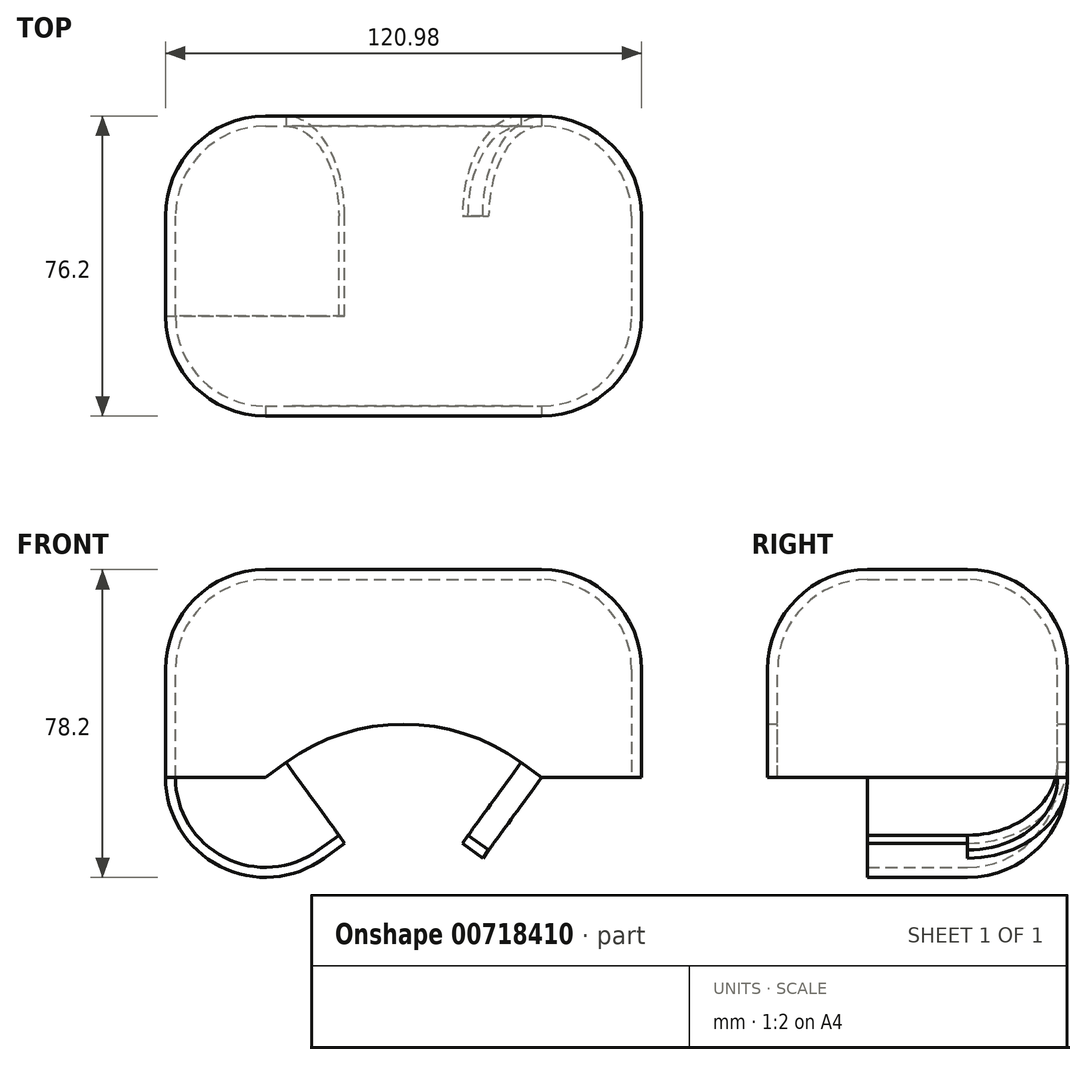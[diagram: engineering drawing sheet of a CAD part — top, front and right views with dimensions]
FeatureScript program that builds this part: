
annotation { "Feature Type Name" : "Feature", "Feature Type Description" : "" }
export const myFeature = defineFeature(function(context is Context, id is Id, definition is map)
    precondition{}
    {
        {
            var Q0;
            Q0=qCreatedBy(makeId("Front.planeOp"),FACE);
            var sketch = newSketch(context, id + "F0", { "sketchPlane" : qUnion([Q0])});
            skLineSegment(sketch, "E0", {"start": v(-60.49, 58.68) * mm, "end": v(60.49, 58.68) * mm});
            skLineSegment(sketch, "E1", {"start": v(60.49, 58.68) * mm, "end": v(60.49, -44) * mm});
            skLineSegment(sketch, "E2", {"start": v(60.49, -44) * mm, "end": v(0, 0) * mm});
            skLineSegment(sketch, "E3", {"start": v(0, 0) * mm, "end": v(-60.49, -44) * mm});
            skLineSegment(sketch, "E4", {"start": v(-60.49, -44) * mm, "end": v(-60.49, 58.68) * mm});
            skSolve(sketch);
        }
        {
            var Q0;
            Q0=makeQuery(id+"F0.imprint","IMPRINT",FACE,{"disambiguationData":[TD([[makeQuery(id+"F0.imprint","IMPRINT",EDGE,{"derivedFrom":sQuery(id+"F0.wireOp",EDGE,"E0")}),-1.0]])]});
            extrude(context, id + "F1", {"entities" : qUnion([Q0]), "depth" : 76.2 * mm, "offsetDistance" : 25.4 * mm});
        }
        {
            var Q0;
            Q0=makeQuery(id+"F1.opExtrude","SWEPT_FACE",FACE,{"disambiguationData":[OSD([sQuery(id+"F0.wireOp",EDGE,"E3")])]});
            var Q1;
            Q1=makeQuery(id+"F1.opExtrude","SWEPT_FACE",FACE,{"disambiguationData":[OSD([sQuery(id+"F0.wireOp",EDGE,"E1")])]});
            var Q2;
            Q2=makeQuery(id+"F1.opExtrude","SWEPT_FACE",FACE,{"disambiguationData":[OSD([sQuery(id+"F0.wireOp",EDGE,"E4")])]});
            var Q3;
            Q3=makeQuery(id+"F1.opExtrude","CAP_FACE",FACE,{"disambiguationData":[OSD([sQuery(id+"F0.wireOp",EDGE,"E0"),sQuery(id+"F0.wireOp",EDGE,"E1"),sQuery(id+"F0.wireOp",EDGE,"E2"),sQuery(id+"F0.wireOp",EDGE,"E3"),sQuery(id+"F0.wireOp",EDGE,"E4")])],"isStart":false});
            var Q4;
            Q4=makeQuery(id+"F1.opExtrude","CAP_FACE",FACE,{"disambiguationData":[OSD([sQuery(id+"F0.wireOp",EDGE,"E0"),sQuery(id+"F0.wireOp",EDGE,"E1"),sQuery(id+"F0.wireOp",EDGE,"E2"),sQuery(id+"F0.wireOp",EDGE,"E3"),sQuery(id+"F0.wireOp",EDGE,"E4")])],"isStart":true});
            var Q5;
            Q5=makeQuery(id+"F1.opExtrude","CAP_EDGE",EDGE,{"disambiguationData":[OSD([sQuery(id+"F0.wireOp",EDGE,"E1")])],"isStart":true});
            var Q6;
            Q6=makeQuery(id+"F1.opExtrude","CAP_EDGE",EDGE,{"disambiguationData":[OSD([sQuery(id+"F0.wireOp",EDGE,"E4")])],"isStart":true});
            var Q7;
            Q7=makeQuery(id+"F1.opExtrude","CAP_EDGE",EDGE,{"disambiguationData":[OSD([sQuery(id+"F0.wireOp",EDGE,"E4")])],"isStart":false});
            var Q8;
            Q8=makeQuery(id+"F1.opExtrude","CAP_EDGE",EDGE,{"disambiguationData":[OSD([sQuery(id+"F0.wireOp",EDGE,"E2")])],"isStart":true});
            var Q9;
            Q9=makeQuery(id+"F1.opExtrude","CAP_EDGE",EDGE,{"disambiguationData":[OSD([sQuery(id+"F0.wireOp",EDGE,"E3")])],"isStart":true});
            var Q10;
            Q10=makeQuery(id+"F1.opExtrude","SWEPT_EDGE",EDGE,{"disambiguationData":[OSD([sQuery(id+"F0.wireOp",EDGE,"E2"),sQuery(id+"F0.wireOp",EDGE,"E3")])]});
            fillet(context, id + "F2", {"entities" : qUnion([Q0, Q1, Q2, Q3, Q4, Q5, Q6, Q7, Q8, Q9, Q10]), "radius" : 25.4 * mm, "tangentPropagation" : true, "allowEdgeOverflow" : false});
        }
        {
            var Q0;
            {var subQ0=sQuery(id+"F0.wireOp",EDGE,"E3");var subQ1=sQuery(id+"F0.wireOp",EDGE,"E2");Q0=makeQuery(id+"F2.opFillet","BLEND_FACE",FACE,{"disambiguationData":[OSD([subQ1,subQ0]),TDD([makeQuery(id+"F1.opExtrude","SWEPT_EDGE",EDGE,{"disambiguationData":[OSD([subQ1,subQ0])]})])]});}
            var Q1;
            {var subQ0=sQuery(id+"F0.wireOp",EDGE,"E3");var subQ1=sQuery(id+"F0.wireOp",EDGE,"E2");Q1=makeQuery(id+"F2.opFillet","BLEND_FACE",FACE,{"disambiguationData":[OSD([subQ1,subQ0]),TDD([makeQuery(id+"F1.opExtrude","CAP_VERTEX",VERTEX,{"disambiguationData":[OSD([subQ1,subQ0])],"isStart":true})])]});}
            var Q2;
            {var subQ0=sQuery(id+"F0.wireOp",EDGE,"E3");var subQ1=sQuery(id+"F0.wireOp",EDGE,"E2");Q2=makeQuery(id+"F2.opFillet","BLEND_FACE",FACE,{"disambiguationData":[OSD([subQ1,subQ0]),TDD([makeQuery(id+"F1.opExtrude","CAP_VERTEX",VERTEX,{"disambiguationData":[OSD([subQ1,subQ0])],"isStart":false})])]});}
            var Q3;
            {var subQ0=sQuery(id+"F0.wireOp",EDGE,"E2");var subQ1=sQuery(id+"F0.wireOp",EDGE,"E1");Q3=makeQuery(id+"F2.opFillet","BLEND_FACE",FACE,{"disambiguationData":[OSD([subQ1,subQ0]),TDD([makeQuery(id+"F1.opExtrude","CAP_VERTEX",VERTEX,{"disambiguationData":[OSD([subQ1,subQ0])],"isStart":false})])]});}
            var Q4;
            Q4=makeQuery(id+"F1.opExtrude","SWEPT_FACE",FACE,{"disambiguationData":[OSD([sQuery(id+"F0.wireOp",EDGE,"E2")])]});
            var Q5;
            {var subQ0=sQuery(id+"F0.wireOp",EDGE,"E2");Q5=makeQuery(id+"F2.opFillet","BLEND_FACE",FACE,{"disambiguationData":[OSD([subQ0]),TDD([makeQuery(id+"F1.opExtrude","CAP_EDGE",EDGE,{"disambiguationData":[OSD([subQ0])],"isStart":false})])]});}
            var Q6;
            {var subQ0=sQuery(id+"F0.wireOp",EDGE,"E2");var subQ1=sQuery(id+"F0.wireOp",EDGE,"E1");Q6=makeQuery(id+"F2.opFillet","BLEND_FACE",FACE,{"disambiguationData":[OSD([subQ1,subQ0]),TDD([makeQuery(id+"F1.opExtrude","CAP_VERTEX",VERTEX,{"disambiguationData":[OSD([subQ1,subQ0])],"isStart":true})])]});}
            var Q7;
            {var subQ0=sQuery(id+"F0.wireOp",EDGE,"E2");var subQ1=sQuery(id+"F0.wireOp",EDGE,"E1");Q7=makeQuery(id+"F2.opFillet","BLEND_FACE",FACE,{"disambiguationData":[OSD([subQ1,subQ0]),TDD([makeQuery(id+"F1.opExtrude","SWEPT_EDGE",EDGE,{"disambiguationData":[OSD([subQ1,subQ0])]})])]});}
            var Q8;
            {var subQ0=sQuery(id+"F0.wireOp",EDGE,"E4");var subQ1=sQuery(id+"F0.wireOp",EDGE,"E3");Q8=makeQuery(id+"F2.opFillet","BLEND_FACE",FACE,{"disambiguationData":[OSD([subQ1,subQ0]),TDD([makeQuery(id+"F1.opExtrude","CAP_VERTEX",VERTEX,{"disambiguationData":[OSD([subQ1,subQ0])],"isStart":false})])]});}
            var Q9;
            {var subQ0=sQuery(id+"F0.wireOp",EDGE,"E3");Q9=makeQuery(id+"F2.opFillet","BLEND_FACE",FACE,{"disambiguationData":[OSD([subQ0]),TDD([makeQuery(id+"F1.opExtrude","CAP_EDGE",EDGE,{"disambiguationData":[OSD([subQ0])],"isStart":false})])]});}
            shell(context, id + "F3", {"entities" : qUnion([Q0, Q1, Q2, Q3, Q4, Q5, Q6, Q7, Q8, Q9]), "thickness" : 2.54 * mm});
        }
    });
